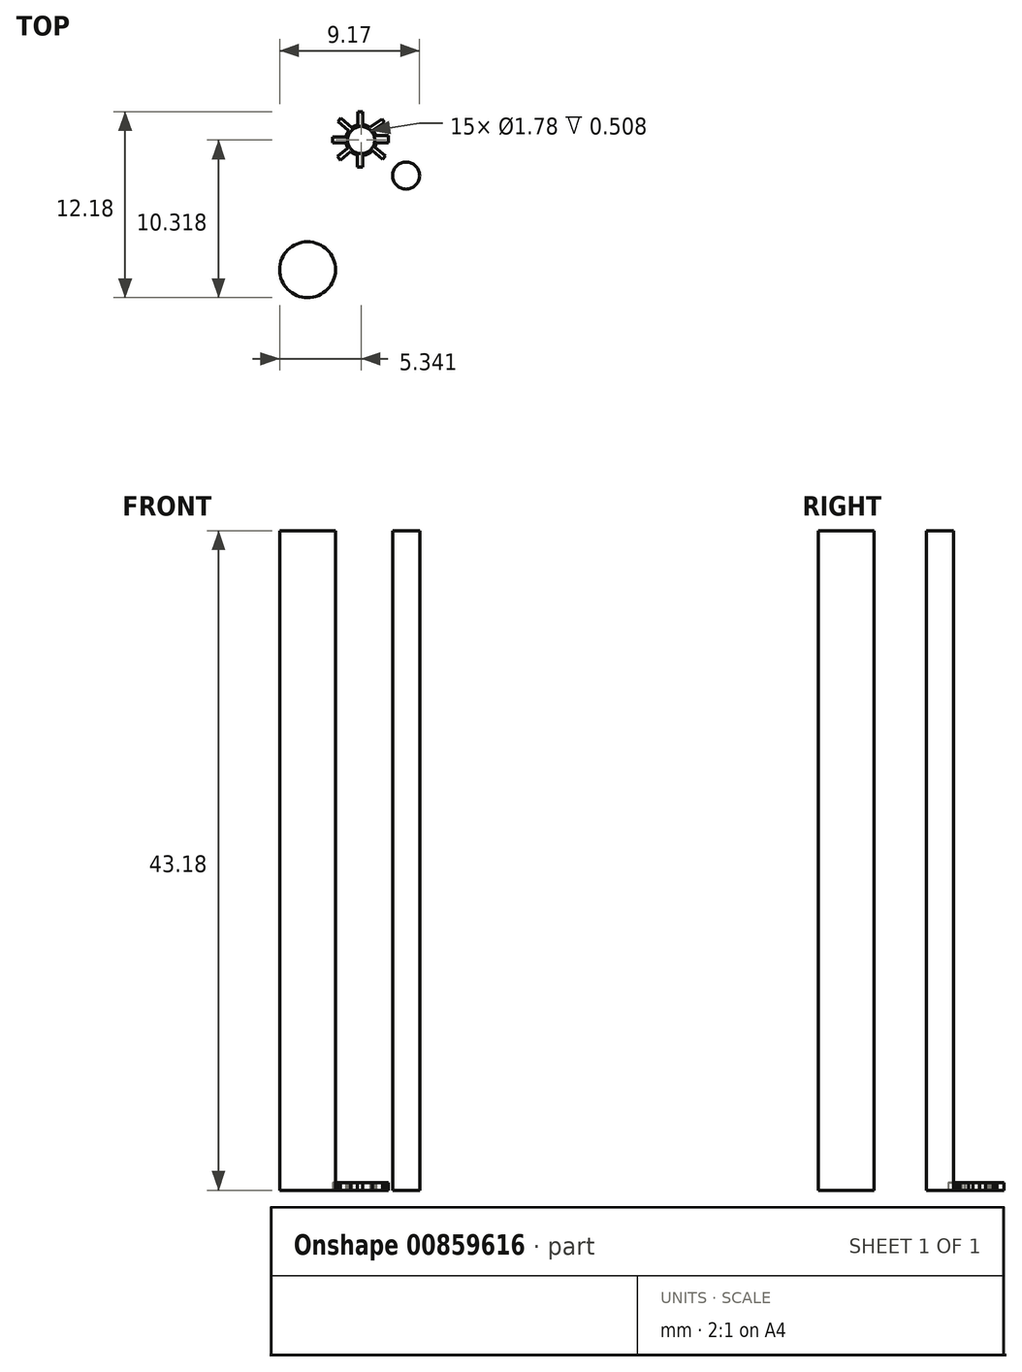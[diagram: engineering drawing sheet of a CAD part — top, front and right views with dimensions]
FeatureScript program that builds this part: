
annotation { "Feature Type Name" : "Feature", "Feature Type Description" : "" }
export const myFeature = defineFeature(function(context is Context, id is Id, definition is map)
    precondition{}
    {
        {
            var Q0;
            Q0=qCreatedBy(makeId("Top.planeOp"),FACE);
            var sketch = newSketch(context, id + "F0", { "sketchPlane" : qUnion([Q0])});
            skCircle(sketch, "E0", {"center": v(0, 0) * mm, "radius": 1.83 * mm});
            skCircle(sketch, "E1", {"center": v(6.45, 6.16) * mm, "radius": 0.89 * mm});
            skCircle(sketch, "E2", {"center": v(3.51, 8.49) * mm, "radius": 1.02 * mm});
            skLineSegment(sketch, "E3", {"start": v(3.28, 9.48) * mm, "end": v(3.28, 10.35) * mm});
            skLineSegment(sketch, "E4", {"start": v(3.28, 10.35) * mm, "end": v(3.61, 10.35) * mm});
            skLineSegment(sketch, "E5", {"start": v(3.61, 10.35) * mm, "end": v(3.61, 9.5) * mm});
            skLineSegment(sketch, "E6", {"start": v(4.49, 8.77) * mm, "end": v(5.3, 8.77) * mm});
            skLineSegment(sketch, "E7", {"start": v(5.3, 8.77) * mm, "end": v(5.3, 8.3) * mm});
            skLineSegment(sketch, "E8", {"start": v(5.3, 8.3) * mm, "end": v(4.51, 8.3) * mm});
            skLineSegment(sketch, "E9", {"start": v(3.61, 7.48) * mm, "end": v(3.61, 6.7) * mm});
            skLineSegment(sketch, "E10", {"start": v(3.61, 6.7) * mm, "end": v(3.28, 6.7) * mm});
            skLineSegment(sketch, "E11", {"start": v(3.28, 6.7) * mm, "end": v(3.28, 7.5) * mm});
            skLineSegment(sketch, "E12", {"start": v(2.51, 8.3) * mm, "end": v(1.64, 8.3) * mm});
            skLineSegment(sketch, "E13", {"start": v(1.64, 8.3) * mm, "end": v(1.64, 8.68) * mm});
            skLineSegment(sketch, "E14", {"start": v(1.64, 8.68) * mm, "end": v(2.51, 8.68) * mm});
            skLineSegment(sketch, "E15", {"start": v(2.7, 9.1) * mm, "end": v(2, 9.71) * mm});
            skLineSegment(sketch, "E16", {"start": v(2, 9.71) * mm, "end": v(2.2, 9.94) * mm});
            skLineSegment(sketch, "E17", {"start": v(2.2, 9.94) * mm, "end": v(2.9, 9.3) * mm});
            skLineSegment(sketch, "E18", {"start": v(4.42, 8.04) * mm, "end": v(5.1, 7.45) * mm});
            skLineSegment(sketch, "E19", {"start": v(5.1, 7.45) * mm, "end": v(4.9, 7.24) * mm});
            skLineSegment(sketch, "E20", {"start": v(4.9, 7.24) * mm, "end": v(4.26, 7.8) * mm});
            skLineSegment(sketch, "E21", {"start": v(4.08, 9.33) * mm, "end": v(4.88, 9.88) * mm});
            skLineSegment(sketch, "E22", {"start": v(4.88, 9.88) * mm, "end": v(5.04, 9.65) * mm});
            skLineSegment(sketch, "E23", {"start": v(5.04, 9.65) * mm, "end": v(4.3, 9.14) * mm});
            skLineSegment(sketch, "E24", {"start": v(2.64, 7.97) * mm, "end": v(1.97, 7.4) * mm});
            skLineSegment(sketch, "E25", {"start": v(1.97, 7.4) * mm, "end": v(2.16, 7.17) * mm});
            skLineSegment(sketch, "E26", {"start": v(2.16, 7.17) * mm, "end": v(2.83, 7.74) * mm});
            skCircle(sketch, "E27", {"center": v(3.51, 8.49) * mm, "radius": 0.89 * mm});
            skSolve(sketch);
        }
        {
            var Q0;
            Q0=makeQuery(id+"F0.imprint","IMPRINT",FACE,{"disambiguationData":[TD([[makeQuery(id+"F0.imprint","IMPRINT",EDGE,{"derivedFrom":sQuery(id+"F0.wireOp",EDGE,"E0")}),1.0]])]});
            extrude(context, id + "F1", {"entities" : qUnion([Q0]), "depth" : 43.18 * mm, "offsetDistance" : 25.4 * mm});
        }
        {
            var Q0;
            Q0=makeQuery(id+"F0.imprint","IMPRINT",FACE,{"disambiguationData":[TD([[makeQuery(id+"F0.imprint","IMPRINT",EDGE,{"derivedFrom":sQuery(id+"F0.wireOp",EDGE,"E1")}),1.0]])]});
            extrude(context, id + "F2", {"entities" : qUnion([Q0]), "depth" : 43.18 * mm, "offsetDistance" : 25.4 * mm});
        }
        {
            var Q0;
            {var subQ0=sQuery(id+"F0.wireOp",EDGE,"E2");var subQ8=makeQuery(id+"F0.imprint","INTERSECT",VERTEX,{"derivedFrom":[subQ0,sQuery(id+"F0.wireOp",EDGE,"E6")]});Q0=makeQuery(id+"F0.imprint","IMPRINT",FACE,{"disambiguationData":[TD([[makeQuery(id+"F0.imprint","IMPRINT",EDGE,{"disambiguationData":[TD([[subQ8,-1.0]])],"derivedFrom":subQ0}),1.0]])]});}
            var Q1;
            {var subQ0=sQuery(id+"F0.wireOp",EDGE,"E3");Q1=makeQuery(id+"F0.imprint","IMPRINT",FACE,{"disambiguationData":[TD([[makeQuery(id+"F0.imprint","IMPRINT",EDGE,{"derivedFrom":subQ0}),-1.0]])]});}
            var Q2;
            {var subQ0=sQuery(id+"F0.wireOp",EDGE,"E15");Q2=makeQuery(id+"F0.imprint","IMPRINT",FACE,{"disambiguationData":[TD([[makeQuery(id+"F0.imprint","IMPRINT",EDGE,{"derivedFrom":subQ0}),-1.0]])]});}
            var Q3;
            {var subQ0=sQuery(id+"F0.wireOp",EDGE,"E21");Q3=makeQuery(id+"F0.imprint","IMPRINT",FACE,{"disambiguationData":[TD([[makeQuery(id+"F0.imprint","IMPRINT",EDGE,{"derivedFrom":subQ0}),-1.0]])]});}
            var Q4;
            {var subQ0=sQuery(id+"F0.wireOp",EDGE,"E6");Q4=makeQuery(id+"F0.imprint","IMPRINT",FACE,{"disambiguationData":[TD([[makeQuery(id+"F0.imprint","IMPRINT",EDGE,{"derivedFrom":subQ0}),-1.0]])]});}
            var Q5;
            {var subQ0=sQuery(id+"F0.wireOp",EDGE,"E18");Q5=makeQuery(id+"F0.imprint","IMPRINT",FACE,{"disambiguationData":[TD([[makeQuery(id+"F0.imprint","IMPRINT",EDGE,{"derivedFrom":subQ0}),-1.0]])]});}
            var Q6;
            {var subQ0=sQuery(id+"F0.wireOp",EDGE,"E9");Q6=makeQuery(id+"F0.imprint","IMPRINT",FACE,{"disambiguationData":[TD([[makeQuery(id+"F0.imprint","IMPRINT",EDGE,{"derivedFrom":subQ0}),-1.0]])]});}
            var Q7;
            {var subQ0=sQuery(id+"F0.wireOp",EDGE,"E12");Q7=makeQuery(id+"F0.imprint","IMPRINT",FACE,{"disambiguationData":[TD([[makeQuery(id+"F0.imprint","IMPRINT",EDGE,{"derivedFrom":subQ0}),-1.0]])]});}
            var Q8;
            {var subQ0=sQuery(id+"F0.wireOp",EDGE,"E24");Q8=makeQuery(id+"F0.imprint","IMPRINT",FACE,{"disambiguationData":[TD([[makeQuery(id+"F0.imprint","IMPRINT",EDGE,{"derivedFrom":subQ0}),1.0]])]});}
            extrude(context, id + "F3", {"entities" : qUnion([Q0, Q1, Q2, Q3, Q4, Q5, Q6, Q7, Q8]), "depth" : 0.5 * mm, "offsetDistance" : 25.4 * mm});
        }
    });
